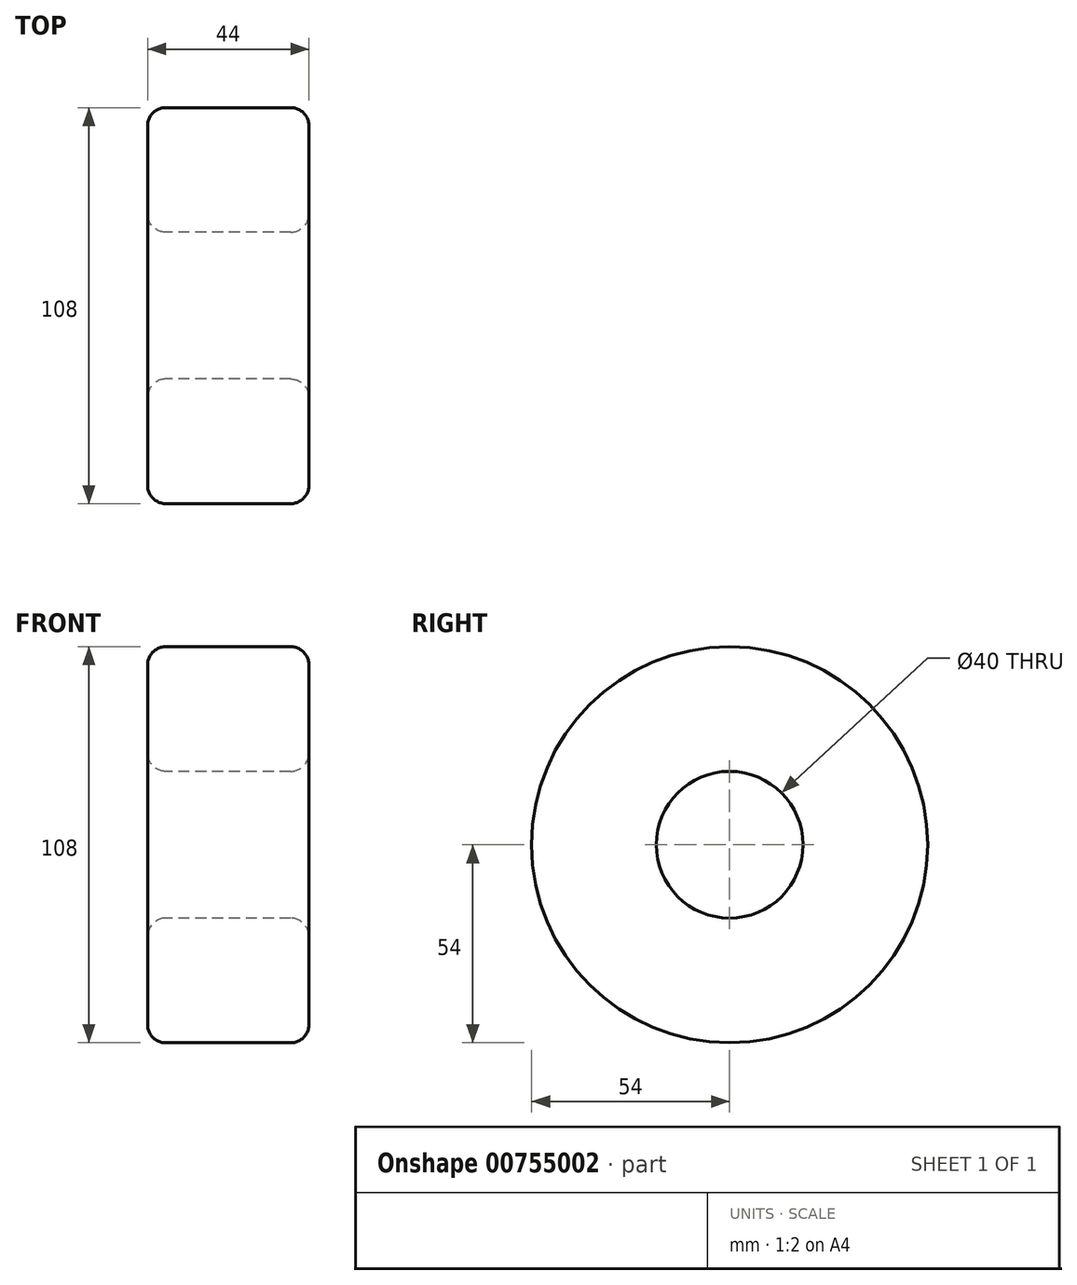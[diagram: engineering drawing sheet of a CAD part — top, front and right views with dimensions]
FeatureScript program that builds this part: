
annotation { "Feature Type Name" : "Feature", "Feature Type Description" : "" }
export const myFeature = defineFeature(function(context is Context, id is Id, definition is map)
    precondition{}
    {
        {
            var Q0;
            Q0=qCreatedBy(makeId("Top.planeOp"),FACE);
            var sketch = newSketch(context, id + "F0", { "sketchPlane" : qUnion([Q0])});
            skLineSegment(sketch, "E0", {"start": v(-21.8, 0) * mm, "end": v(13.32, 0) * mm});
            skLineSegment(sketch, "E1.bottom", {"start": v(-6.8, 54) * mm, "end": v(37.2, 54) * mm});
            skLineSegment(sketch, "E1.top", {"start": v(-6.8, 20) * mm, "end": v(37.2, 20) * mm});
            skLineSegment(sketch, "E1.left", {"start": v(-6.8, 54) * mm, "end": v(-6.8, 20) * mm});
            skLineSegment(sketch, "E1.right", {"start": v(37.2, 54) * mm, "end": v(37.2, 20) * mm});
            skSolve(sketch);
        }
        {
            var Q0;
            Q0 = qSketchRegion(id + "F0", true);
            var Q1;
            Q1=sQuery(id+"F0.wireOp",EDGE,"E0");
            revolve(context, id + "F1", {"surfaceOperationType" : NewSurfaceOperationType.NEW, "entities" : qUnion([Q0]), "axis" : qUnion([Q1]), "revolveType" : RevolveType.FULL});
        }
        {
            var Q0;
            Q0=makeQuery(id+"F1.opRevolve","SWEPT_EDGE",EDGE,{"disambiguationData":[OSD([sQuery(id+"F0.wireOp",EDGE,"E1.bottom"),sQuery(id+"F0.wireOp",EDGE,"E1.left")])]});
            var Q1;
            Q1=makeQuery(id+"F1.opRevolve","SWEPT_EDGE",EDGE,{"disambiguationData":[OSD([sQuery(id+"F0.wireOp",EDGE,"E1.top"),sQuery(id+"F0.wireOp",EDGE,"E1.left")])]});
            var Q2;
            Q2=makeQuery(id+"F1.opRevolve","SWEPT_EDGE",EDGE,{"disambiguationData":[OSD([sQuery(id+"F0.wireOp",EDGE,"E1.top"),sQuery(id+"F0.wireOp",EDGE,"E1.right")])]});
            var Q3;
            Q3=makeQuery(id+"F1.opRevolve","SWEPT_EDGE",EDGE,{"disambiguationData":[OSD([sQuery(id+"F0.wireOp",EDGE,"E1.bottom"),sQuery(id+"F0.wireOp",EDGE,"E1.right")])]});
            fillet(context, id + "F2", {"entities" : qUnion([Q0, Q1, Q2, Q3]), "radius" : 5 * mm, "tangentPropagation" : true, "allowEdgeOverflow" : false});
        }
    });
